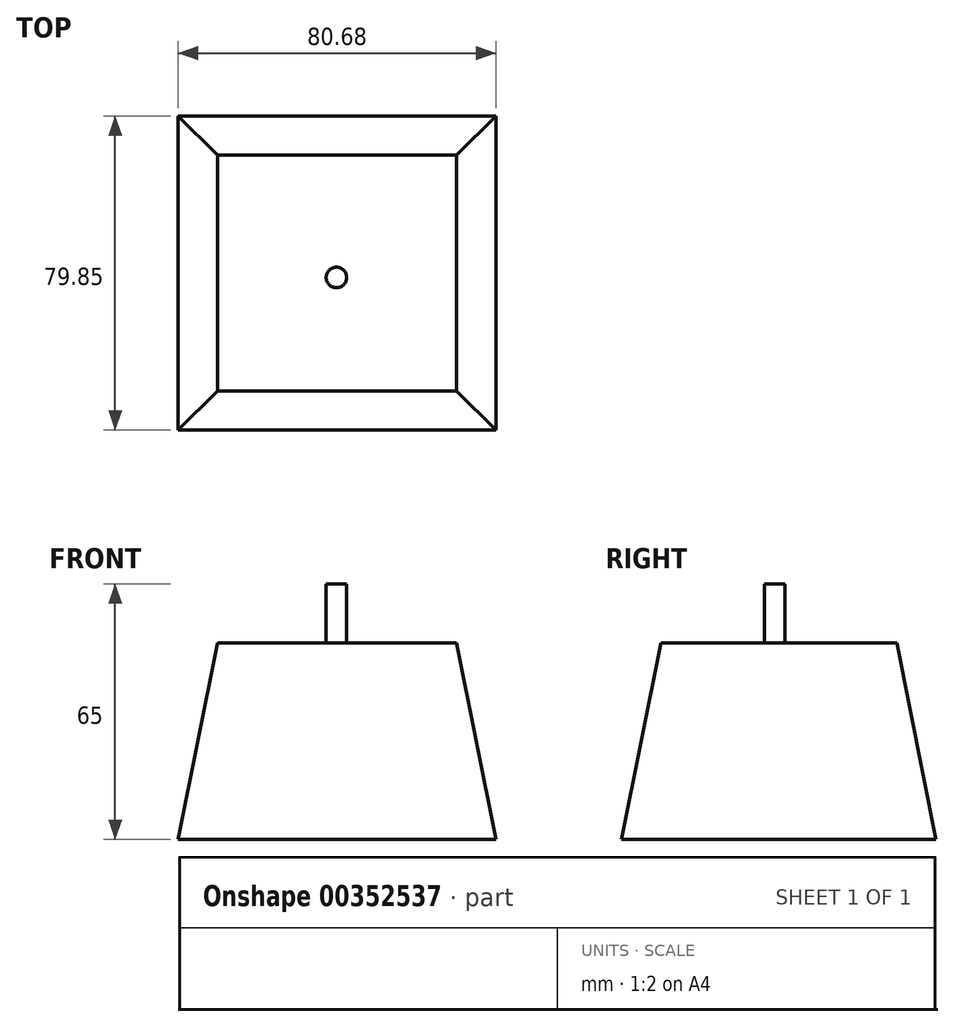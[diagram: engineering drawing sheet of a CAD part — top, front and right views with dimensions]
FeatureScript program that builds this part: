
annotation { "Feature Type Name" : "Feature", "Feature Type Description" : "" }
export const myFeature = defineFeature(function(context is Context, id is Id, definition is map)
    precondition{}
    {
        {
            var Q0;
            Q0=qCreatedBy(makeId("Top.planeOp"),FACE);
            var sketch = newSketch(context, id + "F0", { "sketchPlane" : qUnion([Q0])});
            skLineSegment(sketch, "E0.bottom", {"start": v(-40.2, 41.03) * mm, "end": v(40.48, 41.03) * mm});
            skLineSegment(sketch, "E0.top", {"start": v(-40.2, -38.82) * mm, "end": v(40.48, -38.82) * mm});
            skLineSegment(sketch, "E0.left", {"start": v(-40.2, 41.03) * mm, "end": v(-40.2, -38.82) * mm});
            skLineSegment(sketch, "E0.right", {"start": v(40.48, 41.03) * mm, "end": v(40.48, -38.82) * mm});
            skSolve(sketch);
        }
        {
            var Q0;
            Q0 = qSketchRegion(id + "F0", true);
            extrude(context, id + "F1", {"entities" : qUnion([Q0]), "oppositeDirection" : true, "depth" : 50 * mm});
        }
        {
            var Q0;
            Q0=makeQuery(id+"F1.opExtrude","CAP_FACE",FACE,{"disambiguationData":[OSD([sQuery(id+"F0.wireOp",EDGE,"E0.bottom"),sQuery(id+"F0.wireOp",EDGE,"E0.top"),sQuery(id+"F0.wireOp",EDGE,"E0.left"),sQuery(id+"F0.wireOp",EDGE,"E0.right")])],"isStart":true});
            chamfer(context, id + "F2", {"entities" : qUnion([Q0]), "chamferType" : ChamferType.TWO_OFFSETS, "width1" : 50 * mm, "oppositeDirection" : false, "width2" : 10 * mm, "tangentPropagation" : true});
        }
        {
            var Q0;
            Q0=qCreatedBy(makeId("Top.planeOp"),FACE);
            var sketch = newSketch(context, id + "F3", { "sketchPlane" : qUnion([Q0])});
            skCircle(sketch, "E1", {"center": v(0, 0) * mm, "radius": 2.6 * mm});
            skSolve(sketch);
        }
        {
            var Q0;
            Q0 = qSketchRegion(id + "F3", true);
            extrude(context, id + "F4", {"entities" : qUnion([Q0]), "operationType" : NewBodyOperationType.ADD, "depth" : 15 * mm});
        }
    });
